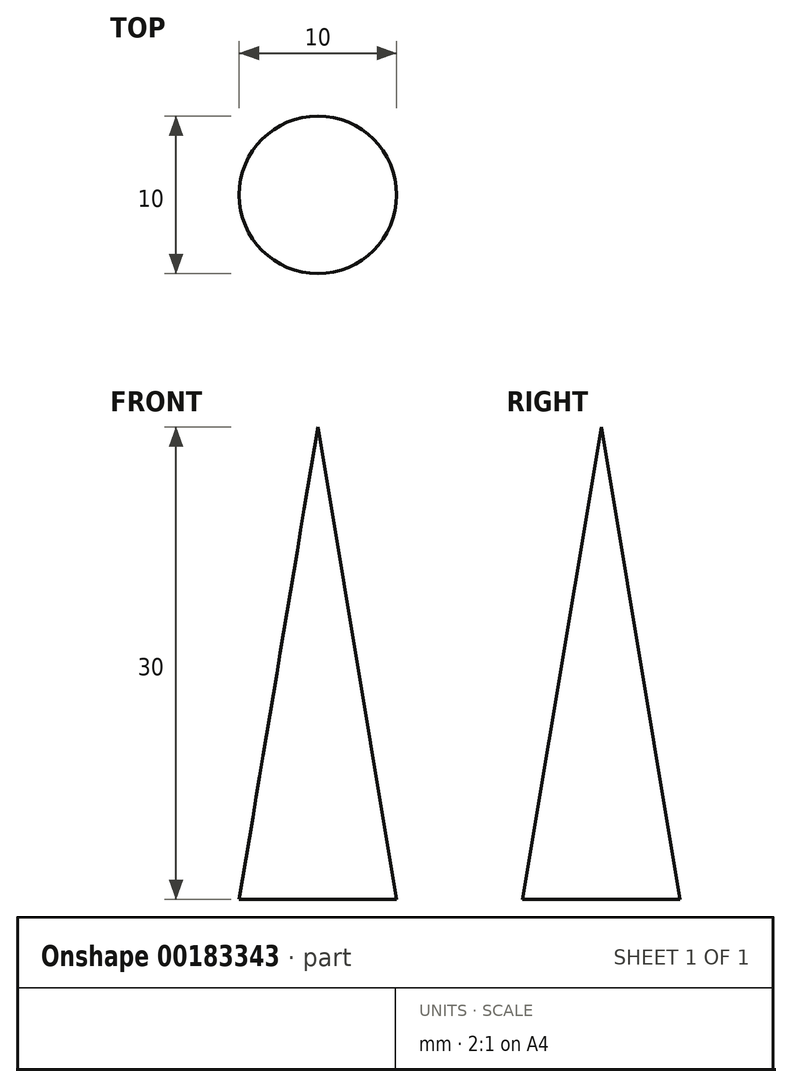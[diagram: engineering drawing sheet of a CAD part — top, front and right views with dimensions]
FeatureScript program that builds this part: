
annotation { "Feature Type Name" : "Feature", "Feature Type Description" : "" }
export const myFeature = defineFeature(function(context is Context, id is Id, definition is map)
    precondition{}
    {
        {
            var Q0;
            Q0=qCreatedBy(makeId("Front.planeOp"),FACE);
            var sketch = newSketch(context, id + "F0", { "sketchPlane" : qUnion([Q0])});
            skLineSegment(sketch, "E0", {"start": v(0, 0) * mm, "end": v(-5, 0) * mm});
            skLineSegment(sketch, "E1", {"start": v(0, 0) * mm, "end": v(0, 30) * mm});
            skLineSegment(sketch, "E2", {"start": v(-5, 0) * mm, "end": v(0, 30) * mm});
            skSolve(sketch);
        }
        {
            var Q0;
            Q0=makeQuery(id+"F0.imprint","IMPRINT",FACE,{"disambiguationData":[TD([[makeQuery(id+"F0.imprint","IMPRINT",EDGE,{"derivedFrom":sQuery(id+"F0.wireOp",EDGE,"E0")}),-1.0]])]});
            var Q1;
            Q1=sQuery(id+"F0.wireOp",EDGE,"E1");
            revolve(context, id + "F1", {"entities" : qUnion([Q0]), "axis" : qUnion([Q1]), "revolveType" : RevolveType.FULL});
        }
    });
